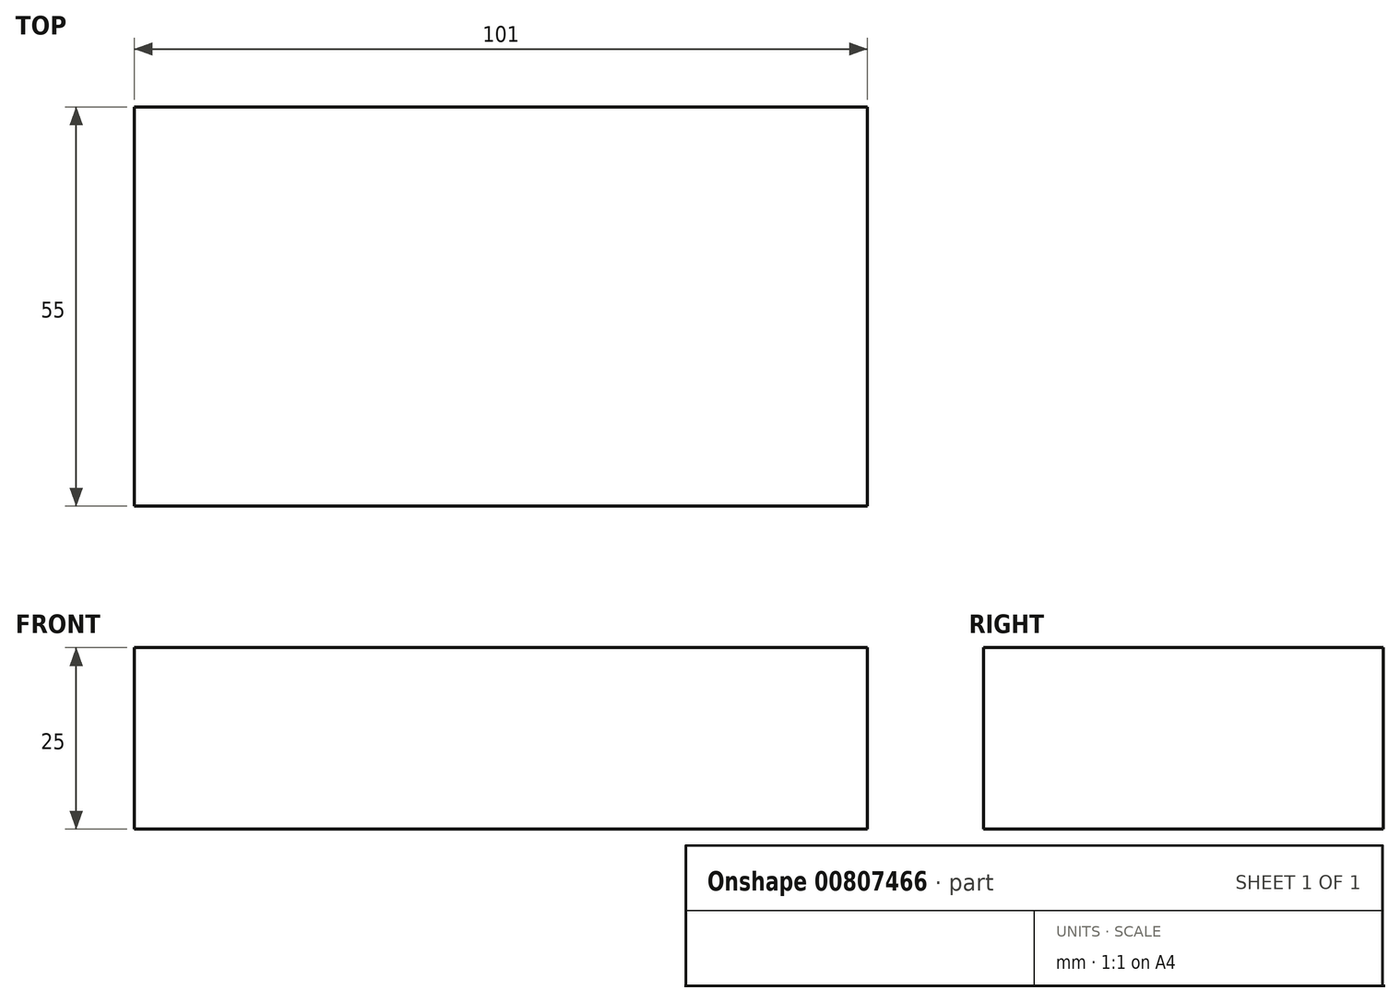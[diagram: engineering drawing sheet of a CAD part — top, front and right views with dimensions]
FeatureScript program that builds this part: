
annotation { "Feature Type Name" : "Feature", "Feature Type Description" : "" }
export const myFeature = defineFeature(function(context is Context, id is Id, definition is map)
    precondition{}
    {
        {
            var Q0;
            Q0=qCreatedBy(makeId("Front.planeOp"),FACE);
            var sketch = newSketch(context, id + "F0", { "sketchPlane" : qUnion([Q0])});
            skLineSegment(sketch, "E0.bottom", {"start": v(-54.22, 12.5) * mm, "end": v(46.78, 12.5) * mm});
            skLineSegment(sketch, "E0.top", {"start": v(-54.22, -12.5) * mm, "end": v(46.78, -12.5) * mm});
            skLineSegment(sketch, "E0.left", {"start": v(-54.22, 12.5) * mm, "end": v(-54.22, -12.5) * mm});
            skLineSegment(sketch, "E0.right", {"start": v(46.78, 12.5) * mm, "end": v(46.78, -12.5) * mm});
            skPoint(sketch, "E0.middle", {"position": v(-3.72, 0) * mm});
            skSolve(sketch);
        }
        {
            var Q0;
            Q0=makeQuery(id+"F0.imprint","IMPRINT",FACE,{"disambiguationData":[TD([[makeQuery(id+"F0.imprint","IMPRINT",EDGE,{"derivedFrom":sQuery(id+"F0.wireOp",EDGE,"E0.bottom")}),-1.0]])]});
            extrude(context, id + "F1", {"entities" : qUnion([Q0]), "depth" : 55 * mm, "offsetDistance" : 25.4 * mm});
        }
    });
